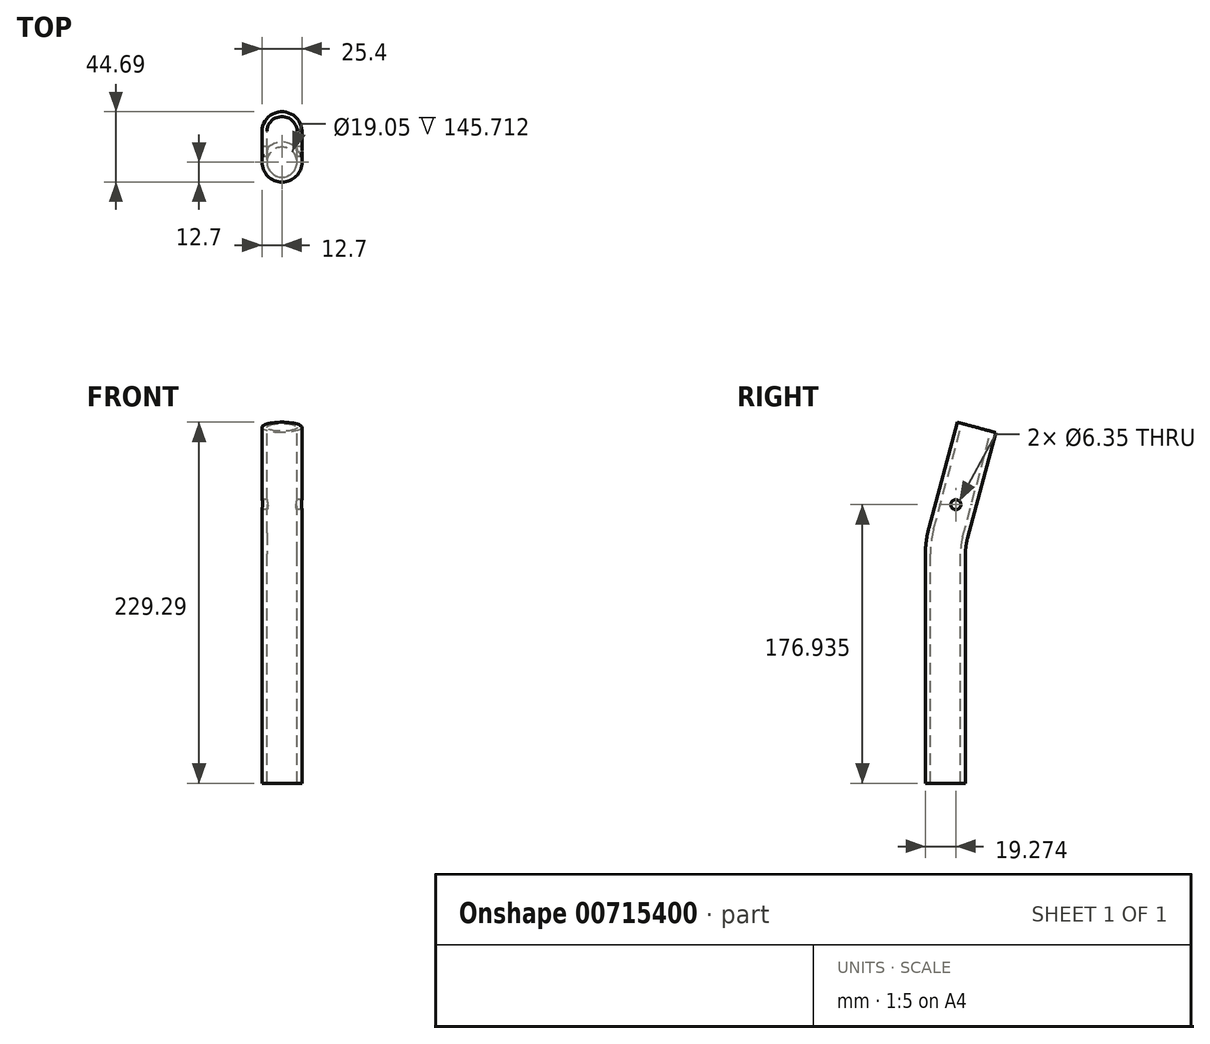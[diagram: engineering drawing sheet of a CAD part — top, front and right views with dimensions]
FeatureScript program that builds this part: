
annotation { "Feature Type Name" : "Feature", "Feature Type Description" : "" }
export const myFeature = defineFeature(function(context is Context, id is Id, definition is map)
    precondition{}
    {
        {
            var Q0;
            Q0=qCreatedBy(makeId("Top.planeOp"),FACE);
            var sketch = newSketch(context, id + "F0", { "sketchPlane" : qUnion([Q0])});
            skCircle(sketch, "E0", {"center": v(0, 0) * mm, "radius": 12.7 * mm});
            skCircle(sketch, "E1.0", {"center": v(0, 0) * mm, "radius": 9.53 * mm});
            skSolve(sketch);
        }
        {
            var Q0;
            Q0=qCreatedBy(makeId("Right.planeOp"),FACE);
            var sketch = newSketch(context, id + "F1", { "sketchPlane" : qUnion([Q0])});
            skLineSegment(sketch, "E2", {"start": v(0, 0) * mm, "end": v(0, 145.71) * mm});
            skLineSegment(sketch, "E3", {"start": v(1.73, 158.86) * mm, "end": v(19.72, 226) * mm});
            skPoint(sketch, "E4.visualSharp", {"position": v(0, 152.4) * mm});
            skArc(sketch, "E4.filletArc", {"start": v(1.73, 158.86) * mm, "mid": v(0.43, 152.34) * mm, "end": v(0, 145.71) * mm});
            skCircle(sketch, "E5", {"center": v(13.15, 201.47) * mm, "radius": 3.18 * mm});
            skCircle(sketch, "E6", {"center": v(6.57, 176.93) * mm, "radius": 3.18 * mm});
            skSolve(sketch);
        }
        {
            var Q0;
            Q0=makeQuery(id+"F0.imprint","IMPRINT",FACE,{"disambiguationData":[TD([[makeQuery(id+"F0.imprint","IMPRINT",EDGE,{"derivedFrom":sQuery(id+"F0.wireOp",EDGE,"E0")}),1.0]])]});
            var Q1;
            Q1=sQuery(id+"F1.wireOp",EDGE,"E2");
            var Q2;
            Q2=sQuery(id+"F1.wireOp",EDGE,"E4.filletArc");
            var Q3;
            Q3=sQuery(id+"F1.wireOp",EDGE,"E3");
            sweep(context, id + "F2", {"profiles" : qUnion([Q0]), "path" : qUnion([Q1, Q2, Q3])});
        }
        {
            var Q0;
            {var subQ0=sQuery(id+"F1.wireOp",EDGE,"E5");var subQ1=sQuery(id+"F1.wireOp",EDGE,"E3");var subQ2=makeQuery(id+"F1.imprint","INTERSECT",VERTEX,{"disambiguationData":[OD(0.0)],"derivedFrom":[subQ1,subQ0]});Q0=makeQuery(id+"F1.imprint","IMPRINT",FACE,{"disambiguationData":[TD([[makeQuery(id+"F1.imprint","IMPRINT",EDGE,{"disambiguationData":[TD([[subQ2,-1.0]])],"derivedFrom":subQ1}),1.0]])]});}
            var Q1;
            {var subQ0=sQuery(id+"F1.wireOp",EDGE,"E5");var subQ1=sQuery(id+"F1.wireOp",EDGE,"E3");var subQ2=makeQuery(id+"F1.imprint","INTERSECT",VERTEX,{"disambiguationData":[OD(0.0)],"derivedFrom":[subQ1,subQ0]});Q1=makeQuery(id+"F1.imprint","IMPRINT",FACE,{"disambiguationData":[TD([[makeQuery(id+"F1.imprint","IMPRINT",EDGE,{"disambiguationData":[TD([[subQ2,-1.0]])],"derivedFrom":subQ1}),-1.0]])]});}
            var Q2;
            {var subQ0=sQuery(id+"F1.wireOp",EDGE,"E6");var subQ1=sQuery(id+"F1.wireOp",EDGE,"E3");var subQ2=makeQuery(id+"F1.imprint","INTERSECT",VERTEX,{"disambiguationData":[OD(0.0)],"derivedFrom":[subQ1,subQ0]});Q2=makeQuery(id+"F1.imprint","IMPRINT",FACE,{"disambiguationData":[TD([[makeQuery(id+"F1.imprint","IMPRINT",EDGE,{"disambiguationData":[TD([[subQ2,-1.0]])],"derivedFrom":subQ1}),-1.0]])]});}
            var Q3;
            {var subQ0=sQuery(id+"F1.wireOp",EDGE,"E6");var subQ1=sQuery(id+"F1.wireOp",EDGE,"E3");var subQ2=makeQuery(id+"F1.imprint","INTERSECT",VERTEX,{"disambiguationData":[OD(0.0)],"derivedFrom":[subQ1,subQ0]});Q3=makeQuery(id+"F1.imprint","IMPRINT",FACE,{"disambiguationData":[TD([[makeQuery(id+"F1.imprint","IMPRINT",EDGE,{"disambiguationData":[TD([[subQ2,-1.0]])],"derivedFrom":subQ1}),1.0]])]});}
            extrude(context, id + "F3", {"entities" : qUnion([Q0, Q1, Q2, Q3]), "operationType" : NewBodyOperationType.REMOVE, "endBound" : BoundingType.SYMMETRIC, "depth" : 50.8 * mm, "offsetDistance" : 25.4 * mm});
        }
    });
